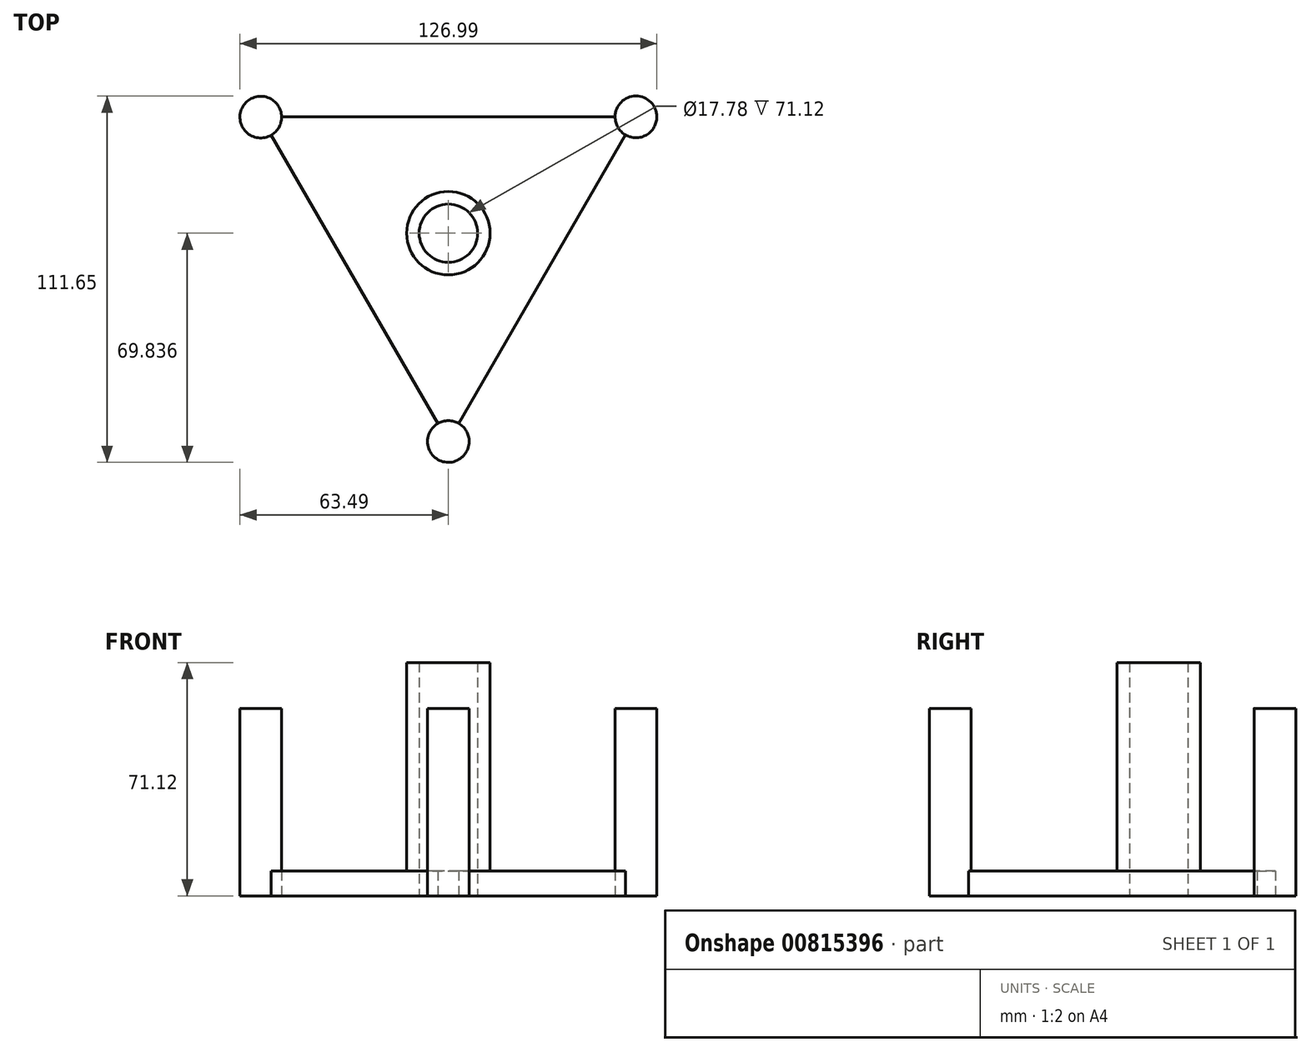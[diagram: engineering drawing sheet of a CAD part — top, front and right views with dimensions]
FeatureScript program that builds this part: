
annotation { "Feature Type Name" : "Feature", "Feature Type Description" : "" }
export const myFeature = defineFeature(function(context is Context, id is Id, definition is map)
    precondition{}
    {
        {
            var Q0;
            Q0=qCreatedBy(makeId("Top.planeOp"),FACE);
            var sketch = newSketch(context, id + "F0", { "sketchPlane" : qUnion([Q0])});
            skLineSegment(sketch, "E0", {"start": v(0, -48.51) * mm, "end": v(-57.15, 50.47) * mm});
            skLineSegment(sketch, "E1", {"start": v(-57.15, 50.47) * mm, "end": v(57.15, 50.47) * mm});
            skLineSegment(sketch, "E2", {"start": v(57.15, 50.47) * mm, "end": v(0, -48.51) * mm});
            skPoint(sketch, "E3.center.orphan", {"position": v(0, 14.99) * mm});
            skSolve(sketch);
        }
        {
            var Q0;
            Q0=qSketchRegion(id+"F0",true);
            extrude(context, id + "F1", {"entities" : qUnion([Q0]), "depth" : 7.62 * mm});
        }
        {
            var Q0;
            Q0=makeQuery(id+"F1.opExtrude","CAP_FACE",FACE,{"disambiguationData":[OSD([sQuery(id+"F0.wireOp",EDGE,"E0"),sQuery(id+"F0.wireOp",EDGE,"E1"),sQuery(id+"F0.wireOp",EDGE,"E2")])],"isStart":false});
            var sketch = newSketch(context, id + "F2", { "sketchPlane" : qUnion([Q0])});
            skCircle(sketch, "E4", {"center": v(0, 14.99) * mm, "radius": 12.7 * mm});
            skSolve(sketch);
        }
        {
            var Q0;
            Q0=qSketchRegion(id+"F2",true);
            extrude(context, id + "F3", {"entities" : qUnion([Q0]), "operationType" : NewBodyOperationType.ADD, "depth" : 63.5 * mm});
        }
        {
            var Q0;
            Q0=qCreatedBy(makeId("Top.planeOp"),FACE);
            var sketch = newSketch(context, id + "F4", { "sketchPlane" : qUnion([Q0])});
            skCircle(sketch, "E5", {"center": v(0, 14.99) * mm, "radius": 8.9 * mm});
            skSolve(sketch);
        }
        {
            var Q0;
            Q0=qSketchRegion(id+"F4",true);
            extrude(context, id + "F5", {"entities" : qUnion([Q0]), "operationType" : NewBodyOperationType.REMOVE, "endBound" : BoundingType.THROUGH_ALL, "depth" : 25.4 * mm});
        }
        {
            var Q0;
            Q0=qCreatedBy(makeId("Top.planeOp"),FACE);
            var sketch = newSketch(context, id + "F6", { "sketchPlane" : qUnion([Q0])});
            skCircle(sketch, "E6", {"center": v(0, -48.5) * mm, "radius": 6.35 * mm});
            skCircle(sketch, "E7", {"center": v(-57.14, 50.38) * mm, "radius": 6.35 * mm});
            skCircle(sketch, "E8", {"center": v(57.15, 50.45) * mm, "radius": 6.35 * mm});
            skSolve(sketch);
        }
        {
            var Q0;
            Q0=qSketchRegion(id+"F6",true);
            extrude(context, id + "F7", {"entities" : qUnion([Q0]), "operationType" : NewBodyOperationType.ADD, "depth" : 57.15 * mm});
        }
    });
